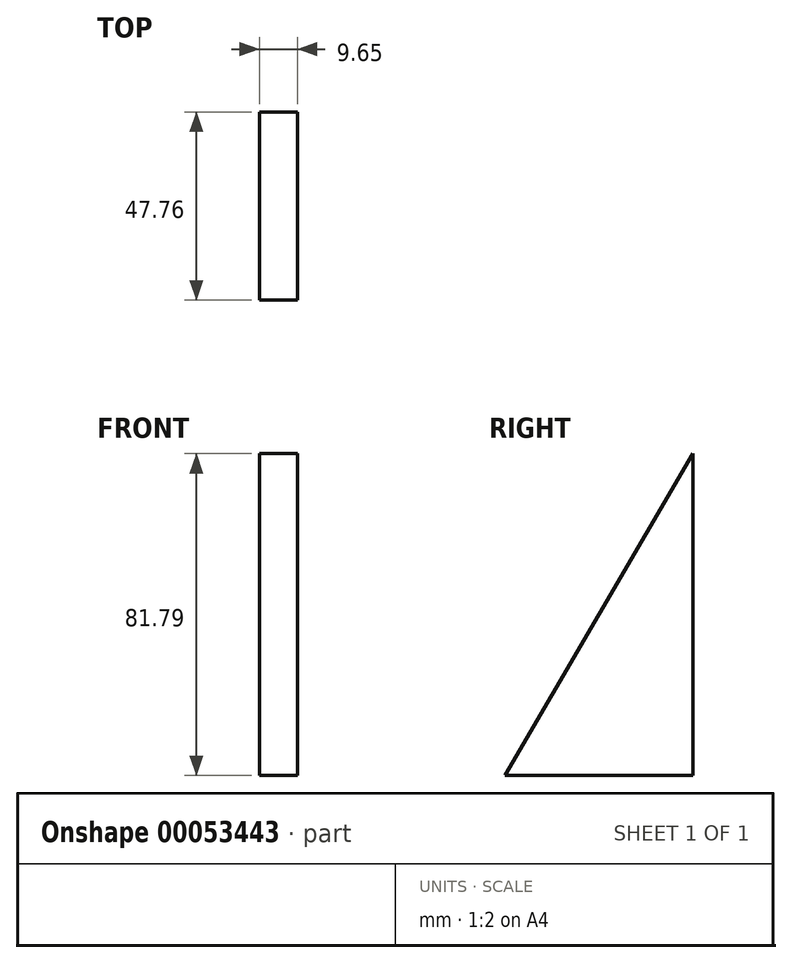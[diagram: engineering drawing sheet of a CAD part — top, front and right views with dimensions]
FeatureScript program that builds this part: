
annotation { "Feature Type Name" : "Feature", "Feature Type Description" : "" }
export const myFeature = defineFeature(function(context is Context, id is Id, definition is map)
    precondition{}
    {
        {
            var Q0;
            Q0=qCreatedBy(makeId("Right.planeOp"),FACE);
            var sketch = newSketch(context, id + "F0", { "sketchPlane" : qUnion([Q0])});
            skLineSegment(sketch, "E0", {"start": v(-33.21, 74.6) * mm, "end": v(-33.21, -7.19) * mm});
            skLineSegment(sketch, "E1", {"start": v(-33.21, -7.19) * mm, "end": v(-80.97, -7.19) * mm});
            skLineSegment(sketch, "E2", {"start": v(-80.97, -7.19) * mm, "end": v(-33.21, 74.6) * mm});
            skLineSegment(sketch, "E3", {"start": v(-80.97, -7.19) * mm, "end": v(-33.21, -7.19) * mm});
            skSolve(sketch);
        }
        {
            var Q0;
            Q0=makeQuery(id+"F0.imprint","IMPRINT",FACE,{"disambiguationData":[TD([[makeQuery(id+"F0.imprint","IMPRINT",EDGE,{"derivedFrom":sQuery(id+"F0.wireOp",EDGE,"E0")}),-1.0]])]});
            extrude(context, id + "F1", {"entities" : qUnion([Q0]), "depth" : 9.65 * mm});
        }
    });
